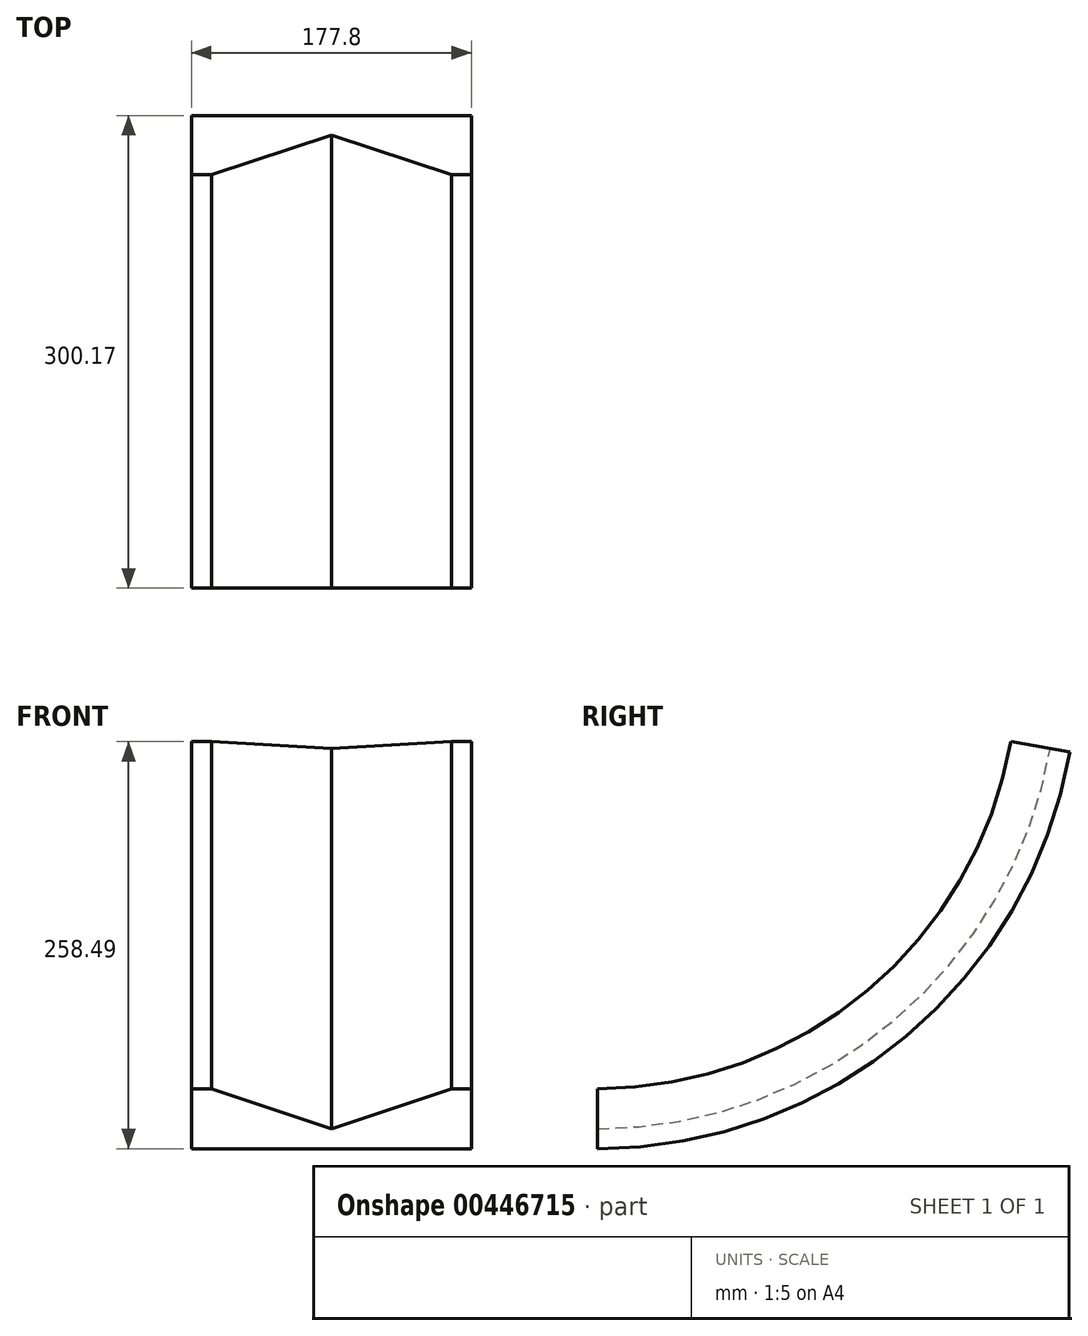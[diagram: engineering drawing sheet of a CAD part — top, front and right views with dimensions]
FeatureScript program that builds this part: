
annotation { "Feature Type Name" : "Feature", "Feature Type Description" : "" }
export const myFeature = defineFeature(function(context is Context, id is Id, definition is map)
    precondition{}
    {
        {
            var Q0;
            Q0=qCreatedBy(makeId("Front.planeOp"),FACE);
            var sketch = newSketch(context, id + "F0", { "sketchPlane" : qUnion([Q0])});
            skLineSegment(sketch, "E0", {"start": v(0, 0) * mm, "end": v(177.8, 0) * mm});
            skLineSegment(sketch, "E1", {"start": v(177.8, 0) * mm, "end": v(177.8, 38.1) * mm});
            skLineSegment(sketch, "E2", {"start": v(177.8, 38.1) * mm, "end": v(165.1, 38.1) * mm});
            skLineSegment(sketch, "E3", {"start": v(88.9, 12.7) * mm, "end": v(88.9, 12.7) * mm});
            skLineSegment(sketch, "E4", {"start": v(12.7, 38.1) * mm, "end": v(0, 38.1) * mm});
            skLineSegment(sketch, "E5", {"start": v(0, 38.1) * mm, "end": v(0, 0) * mm});
            skLineSegment(sketch, "E6", {"start": v(12.7, 38.1) * mm, "end": v(88.9, 12.7) * mm});
            skLineSegment(sketch, "E7", {"start": v(165.1, 38.1) * mm, "end": v(88.9, 12.7) * mm});
            skSolve(sketch);
        }
        {
            var Q0;
            Q0=qCreatedBy(makeId("Front.planeOp"),FACE);
            var sketch = newSketch(context, id + "F1", { "sketchPlane" : qUnion([Q0])});
            skLineSegment(sketch, "E8", {"start": v(0, 304.8) * mm, "end": v(232.83, 304.8) * mm, "construction": true});
            skSolve(sketch);
        }
        {
            var Q0;
            Q0 = qSketchRegion(id + "F0", true);
            var Q1;
            Q1=sQuery(id+"F1.wireOp",EDGE,"E8");
            revolve(context, id + "F2", {"entities" : qUnion([Q0]), "axis" : qUnion([Q1]), "revolveType" : RevolveType.ONE_DIRECTION, "angle" : 80 * degree});
        }
    });
